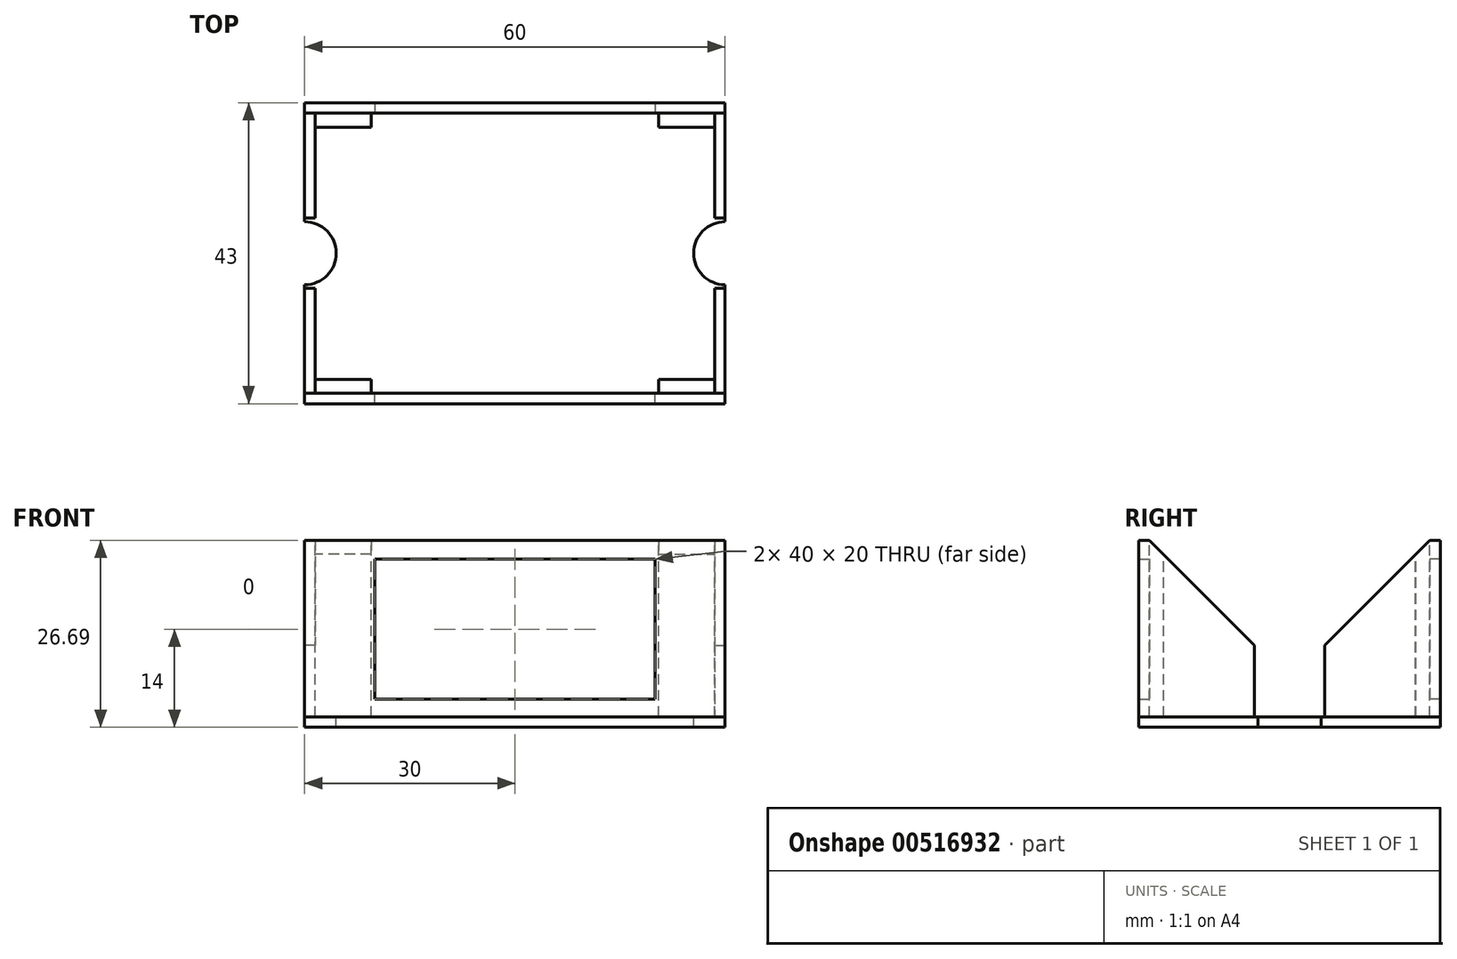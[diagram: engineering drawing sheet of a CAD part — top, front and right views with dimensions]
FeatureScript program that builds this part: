
annotation { "Feature Type Name" : "Feature", "Feature Type Description" : "" }
export const myFeature = defineFeature(function(context is Context, id is Id, definition is map)
    precondition{}
    {
        {
            var Q0;
            Q0=qCreatedBy(makeId("Front.planeOp"),FACE);
            var sketch = newSketch(context, id + "F0", { "sketchPlane" : qUnion([Q0])});
            skLineSegment(sketch, "E0.bottom", {"start": v(-25, 0) * mm, "end": v(-2.5, 0) * mm});
            skLineSegment(sketch, "E0.top", {"start": v(-28.49, 25.2) * mm, "end": v(28.24, 25.2) * mm});
            skLineSegment(sketch, "E0.left", {"start": v(-30, 0) * mm, "end": v(-30, 15.2) * mm});
            skLineSegment(sketch, "E0.right", {"start": v(30, 0) * mm, "end": v(30, 15.2) * mm});
            skLineSegment(sketch, "E1.bottom", {"start": v(-20, 22.5) * mm, "end": v(20, 22.5) * mm});
            skLineSegment(sketch, "E1.top", {"start": v(-20, 2.5) * mm, "end": v(20, 2.5) * mm});
            skLineSegment(sketch, "E1.left", {"start": v(-20, 22.5) * mm, "end": v(-20, 2.5) * mm});
            skLineSegment(sketch, "E1.right", {"start": v(20, 22.5) * mm, "end": v(20, 2.5) * mm});
            skLineSegment(sketch, "E2.trimOffspring", {"start": v(2.5, 0) * mm, "end": v(25, 0) * mm});
            skLineSegment(sketch, "E3", {"start": v(-30, 15.2) * mm, "end": v(-30, 25.2) * mm});
            skLineSegment(sketch, "E4", {"start": v(-30, 25.2) * mm, "end": v(-28.49, 25.2) * mm});
            skLineSegment(sketch, "E5", {"start": v(30, 15.2) * mm, "end": v(30, 25.2) * mm});
            skLineSegment(sketch, "E6", {"start": v(30, 25.2) * mm, "end": v(28.24, 25.2) * mm});
            skLineSegment(sketch, "E7", {"start": v(30, 0) * mm, "end": v(25, 0) * mm});
            skLineSegment(sketch, "E8", {"start": v(2.5, 0) * mm, "end": v(-2.5, 0) * mm});
            skLineSegment(sketch, "E9", {"start": v(-25, 0) * mm, "end": v(-30, 0) * mm});
            skSolve(sketch);
        }
        {
            var Q0;
            Q0 = qSketchRegion(id + "F0", true);
            extrude(context, id + "F1", {"entities" : qUnion([Q0]), "depth" : 1.5 * mm, "offsetDistance" : 25 * mm});
        }
        {
            var Q0;
            Q0=makeQuery(id+"F1.opExtrude","SWEPT_FACE",FACE,{"disambiguationData":[OSD([sQuery(id+"F0.wireOp",EDGE,"E0.left"),sQuery(id+"F0.wireOp",EDGE,"E3")])]});
            var sketch = newSketch(context, id + "F2", { "sketchPlane" : qUnion([Q0])});
            skLineSegment(sketch, "E10", {"start": v(0, 0) * mm, "end": v(0, 25.2) * mm});
            skLineSegment(sketch, "E11", {"start": v(0, 25.2) * mm, "end": v(-15, 10.2) * mm});
            skLineSegment(sketch, "E12", {"start": v(-15, 0) * mm, "end": v(0, 0) * mm});
            skLineSegment(sketch, "E13", {"start": v(-15, 0) * mm, "end": v(-15, 10.2) * mm});
            skPoint(sketch, "E14.orphan", {"position": v(-25.2, 0) * mm});
            skSolve(sketch);
        }
        {
            var Q0;
            Q0 = qSketchRegion(id + "F2", true);
            extrude(context, id + "F3", {"entities" : qUnion([Q0]), "oppositeDirection" : true, "depth" : 1.5 * mm, "offsetDistance" : 25 * mm});
        }
        {
            var Q0;
            Q0=makeQuery(id+"F1.opExtrude","SWEPT_FACE",FACE,{"disambiguationData":[OSD([sQuery(id+"F0.wireOp",EDGE,"E0.right"),sQuery(id+"F0.wireOp",EDGE,"E5")])]});
            var sketch = newSketch(context, id + "F4", { "sketchPlane" : qUnion([Q0])});
            skLineSegment(sketch, "E15", {"start": v(0, 0) * mm, "end": v(0, 25.2) * mm});
            skLineSegment(sketch, "E16", {"start": v(0, 25.2) * mm, "end": v(15, 10.2) * mm});
            skLineSegment(sketch, "E17", {"start": v(15, 10.2) * mm, "end": v(15, 0) * mm});
            skLineSegment(sketch, "E18", {"start": v(15, 0) * mm, "end": v(0, 0) * mm});
            skSolve(sketch);
        }
        {
            var Q0;
            Q0 = qSketchRegion(id + "F4", true);
            extrude(context, id + "F5", {"entities" : qUnion([Q0]), "operationType" : NewBodyOperationType.ADD, "oppositeDirection" : true, "depth" : 1.5 * mm, "offsetDistance" : 25 * mm});
        }
        {
            var Q0;
            Q0=makeQuery(id+"F3.opExtrude","SWEPT_FACE",FACE,{"disambiguationData":[OSD([sQuery(id+"F2.wireOp",EDGE,"E13")])]});
            cPlane(context, id + "F6", {"entities" : qUnion([Q0]), "cplaneType" : CPlaneType.OFFSET, "offset" : 5 * mm, "width" : 150 * mm, "height" : 150 * mm});
        }
        {
            var Q0;
            Q0=makeQuery(id+"F3.opExtrude","CAP_FACE",FACE,{"disambiguationData":[OSD([sQuery(id+"F2.wireOp",EDGE,"E10"),sQuery(id+"F2.wireOp",EDGE,"E11"),sQuery(id+"F2.wireOp",EDGE,"E12"),sQuery(id+"F2.wireOp",EDGE,"E13")])],"isStart":false});
            var sketch = newSketch(context, id + "F7", { "sketchPlane" : qUnion([Q0])});
            skLineSegment(sketch, "E19.bottom", {"start": v(0, 0) * mm, "end": v(2, 0) * mm});
            skLineSegment(sketch, "E19.left", {"start": v(0, 0) * mm, "end": v(0, 25.2) * mm});
            skLineSegment(sketch, "E19.right", {"start": v(2, 0) * mm, "end": v(2, 23.2) * mm});
            skLineSegment(sketch, "E20", {"start": v(2, 23.2) * mm, "end": v(0, 25.2) * mm});
            skSolve(sketch);
        }
        {
            var Q0;
            Q0=makeQuery(id+"F7.imprint","IMPRINT",FACE,{"disambiguationData":[TD([[makeQuery(id+"F7.imprint","IMPRINT",EDGE,{"derivedFrom":sQuery(id+"F7.wireOp",EDGE,"E19.bottom")}),-1.0]])]});
            extrude(context, id + "F8", {"entities" : qUnion([Q0]), "depth" : 8 * mm, "offsetDistance" : 25 * mm});
        }
        {
            var Q0;
            Q0=makeQuery(id+"F5.opExtrude","CAP_FACE",FACE,{"disambiguationData":[OSD([sQuery(id+"F4.wireOp",EDGE,"E15"),sQuery(id+"F4.wireOp",EDGE,"E16"),sQuery(id+"F4.wireOp",EDGE,"E17"),sQuery(id+"F4.wireOp",EDGE,"E18")])],"isStart":false});
            var sketch = newSketch(context, id + "F9", { "sketchPlane" : qUnion([Q0])});
            skLineSegment(sketch, "E21.bottom", {"start": v(0, 0) * mm, "end": v(-2, 0) * mm});
            skLineSegment(sketch, "E21.left", {"start": v(0, 0) * mm, "end": v(0, 25.2) * mm});
            skLineSegment(sketch, "E21.right", {"start": v(-2, 0) * mm, "end": v(-2, 23.2) * mm});
            skLineSegment(sketch, "E22", {"start": v(0, 25.2) * mm, "end": v(-2, 23.2) * mm});
            skPoint(sketch, "E21.top.end.orphan", {"position": v(-2, 25.2) * mm});
            skSolve(sketch);
        }
        {
            var Q0;
            Q0=makeQuery(id+"F9.imprint","IMPRINT",FACE,{"disambiguationData":[TD([[makeQuery(id+"F9.imprint","IMPRINT",EDGE,{"derivedFrom":sQuery(id+"F9.wireOp",EDGE,"E21.bottom")}),1.0]])]});
            extrude(context, id + "F10", {"entities" : qUnion([Q0]), "depth" : 8 * mm, "offsetDistance" : 25 * mm});
        }
        {
            var Q0;
            Q0=makeQuery(id+"F1.opExtrude","SWEPT_BODY",BODY,{"disambiguationData":[OSD([sQuery(id+"F0.wireOp",EDGE,"E0.bottom"),sQuery(id+"F0.wireOp",EDGE,"E0.top"),sQuery(id+"F0.wireOp",EDGE,"E0.left"),sQuery(id+"F0.wireOp",EDGE,"E0.right"),sQuery(id+"F0.wireOp",EDGE,"E1.bottom"),sQuery(id+"F0.wireOp",EDGE,"E1.top"),sQuery(id+"F0.wireOp",EDGE,"E1.left"),sQuery(id+"F0.wireOp",EDGE,"E1.right"),sQuery(id+"F0.wireOp",EDGE,"E2.trimOffspring"),sQuery(id+"F0.wireOp",EDGE,"E3"),sQuery(id+"F0.wireOp",EDGE,"E4"),sQuery(id+"F0.wireOp",EDGE,"E5"),sQuery(id+"F0.wireOp",EDGE,"E6"),sQuery(id+"F0.wireOp",EDGE,"E7"),sQuery(id+"F0.wireOp",EDGE,"E8"),sQuery(id+"F0.wireOp",EDGE,"E9")])]});
            var Q1;
            Q1=makeQuery(id+"F8.opExtrude","SWEPT_BODY",BODY,{"disambiguationData":[OSD([sQuery(id+"F7.wireOp",EDGE,"E19.bottom"),sQuery(id+"F7.wireOp",EDGE,"E19.left"),sQuery(id+"F7.wireOp",EDGE,"E19.right"),sQuery(id+"F7.wireOp",EDGE,"E20")])]});
            var Q2;
            Q2=makeQuery(id+"F3.opExtrude","SWEPT_BODY",BODY,{"disambiguationData":[OSD([sQuery(id+"F2.wireOp",EDGE,"E10"),sQuery(id+"F2.wireOp",EDGE,"E11"),sQuery(id+"F2.wireOp",EDGE,"E12"),sQuery(id+"F2.wireOp",EDGE,"E13")])]});
            var Q3;
            Q3=makeQuery(id+"F10.opExtrude","SWEPT_BODY",BODY,{"disambiguationData":[OSD([sQuery(id+"F9.wireOp",EDGE,"E21.bottom"),sQuery(id+"F9.wireOp",EDGE,"E21.left"),sQuery(id+"F9.wireOp",EDGE,"E21.right"),sQuery(id+"F9.wireOp",EDGE,"E22")])]});
            var Q4;
            Q4=qCreatedBy(id+"F6.planeOp",FACE);
            mirror(context, id + "F11", {"entities" : qUnion([Q0, Q1, Q2, Q3]), "mirrorPlane" : qUnion([Q4])});
        }
        {
            var Q0;
            Q0=makeQuery(id+"F5.boolean.opBoolean","MERGE",FACE,{"derivedFrom":[makeQuery(id+"F1.opExtrude","SWEPT_FACE",FACE,{"disambiguationData":[OSD([sQuery(id+"F0.wireOp",EDGE,"E0.bottom"),sQuery(id+"F0.wireOp",EDGE,"E2.trimOffspring"),sQuery(id+"F0.wireOp",EDGE,"E7"),sQuery(id+"F0.wireOp",EDGE,"E8"),sQuery(id+"F0.wireOp",EDGE,"E9")])]}),makeQuery(id+"F5.opExtrude","SWEPT_FACE",FACE,{"disambiguationData":[OSD([sQuery(id+"F4.wireOp",EDGE,"E18")])]})]});
            var sketch = newSketch(context, id + "F12", { "sketchPlane" : qUnion([Q0])});
            skLineSegment(sketch, "E23.bottom", {"start": v(-30, 1.5) * mm, "end": v(30, 1.5) * mm});
            skLineSegment(sketch, "E23.top", {"start": v(-30, -41.5) * mm, "end": v(30, -41.5) * mm});
            skLineSegment(sketch, "E23.left", {"start": v(-30, 1.5) * mm, "end": v(-30, -15.5) * mm});
            skLineSegment(sketch, "E23.right", {"start": v(30, 1.5) * mm, "end": v(30, -15.5) * mm});
            skArc(sketch, "E24", {"start": v(30, -15.5) * mm, "mid": v(25.5, -20) * mm, "end": v(30, -24.5) * mm});
            skArc(sketch, "E25", {"start": v(-30, -24.5) * mm, "mid": v(-25.5, -20) * mm, "end": v(-30, -15.5) * mm});
            skLineSegment(sketch, "E26.trimOffspring", {"start": v(30, -24.5) * mm, "end": v(30, -41.5) * mm});
            skLineSegment(sketch, "E27.trimOffspring", {"start": v(-30, -24.5) * mm, "end": v(-30, -41.5) * mm});
            skSolve(sketch);
        }
        {
            var Q0;
            Q0 = qSketchRegion(id + "F12", true);
            extrude(context, id + "F13", {"entities" : qUnion([Q0]), "depth" : 1.5 * mm, "offsetDistance" : 25 * mm});
        }
    });
